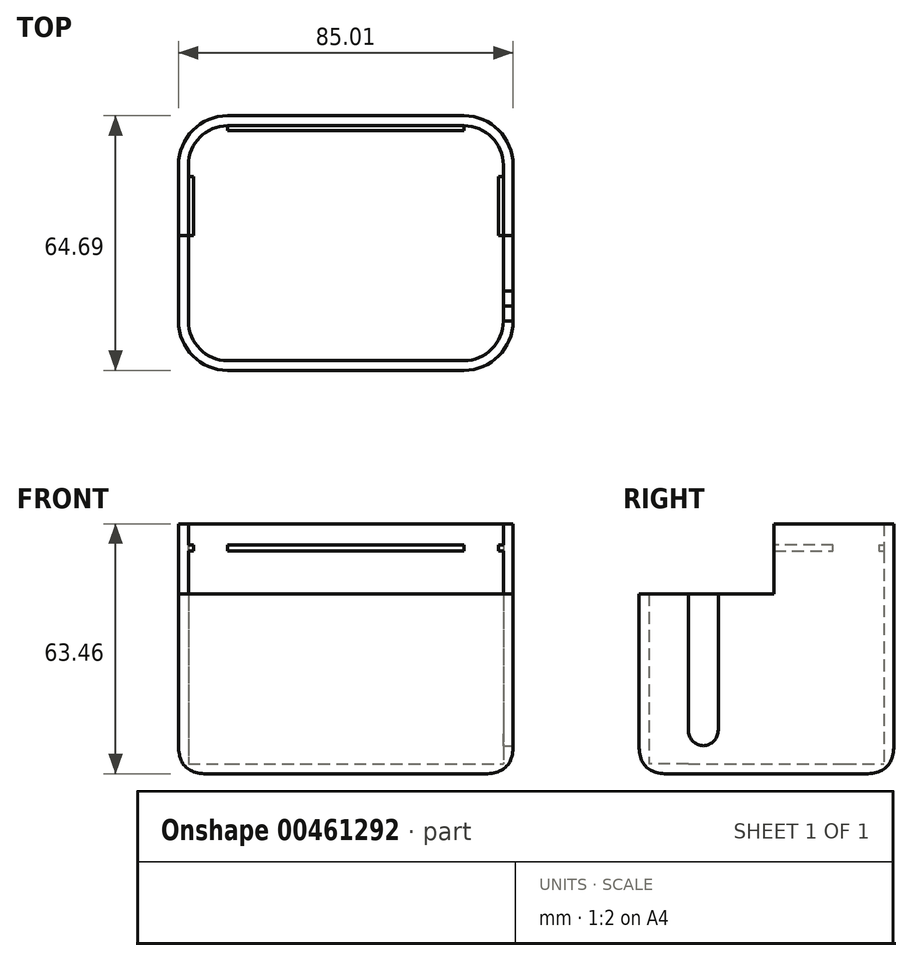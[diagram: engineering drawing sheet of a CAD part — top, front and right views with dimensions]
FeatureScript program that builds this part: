
annotation { "Feature Type Name" : "Feature", "Feature Type Description" : "" }
export const myFeature = defineFeature(function(context is Context, id is Id, definition is map)
    precondition{}
    {
        {
            var Q0;
            Q0=qCreatedBy(makeId("Top.planeOp"),FACE);
            var sketch = newSketch(context, id + "F0", { "sketchPlane" : qUnion([Q0])});
            skLineSegment(sketch, "E0.bottom", {"start": v(10, 0) * mm, "end": v(70.01, 0) * mm});
            skLineSegment(sketch, "E0.top", {"start": v(10, 59.7) * mm, "end": v(70.01, 59.7) * mm});
            skLineSegment(sketch, "E0.left", {"start": v(0, 10) * mm, "end": v(0, 49.7) * mm});
            skLineSegment(sketch, "E0.right", {"start": v(80.01, 10) * mm, "end": v(80.01, 49.7) * mm});
            skPoint(sketch, "E1.visualSharp", {"position": v(0, 59.7) * mm});
            skArc(sketch, "E1.filletArc", {"start": v(10, 59.7) * mm, "mid": v(2.93, 56.76) * mm, "end": v(0, 49.7) * mm});
            skPoint(sketch, "E2.visualSharp", {"position": v(0, 0) * mm});
            skArc(sketch, "E2.filletArc", {"start": v(0, 10) * mm, "mid": v(2.93, 2.93) * mm, "end": v(10, 0) * mm});
            skPoint(sketch, "E3.visualSharp", {"position": v(80.01, 0) * mm});
            skArc(sketch, "E3.filletArc", {"start": v(70.01, 0) * mm, "mid": v(77.08, 2.93) * mm, "end": v(80.01, 10) * mm});
            skPoint(sketch, "E4.visualSharp", {"position": v(80, 59.7) * mm});
            skArc(sketch, "E4.filletArc", {"start": v(80, 49.7) * mm, "mid": v(77.08, 56.76) * mm, "end": v(70.01, 59.7) * mm});
            skSolve(sketch);
        }
        {
            var Q0;
            Q0=makeQuery(id+"F0.imprint","IMPRINT",FACE,{"disambiguationData":[TD([[makeQuery(id+"F0.imprint","IMPRINT",EDGE,{"derivedFrom":sQuery(id+"F0.wireOp",EDGE,"E0.bottom")}),1.0]])]});
            extrude(context, id + "F1", {"entities" : qUnion([Q0]), "depth" : 60.96 * mm});
        }
        {
            var Q0;
            Q0=makeQuery(id+"F1.opExtrude","CAP_FACE",FACE,{"disambiguationData":[OSD([sQuery(id+"F0.wireOp",EDGE,"E0.bottom"),sQuery(id+"F0.wireOp",EDGE,"E0.top"),sQuery(id+"F0.wireOp",EDGE,"E0.left"),sQuery(id+"F0.wireOp",EDGE,"E0.right")])],"isStart":false});
            shell(context, id + "F2", {"entities" : qUnion([Q0]), "thickness" : 2.5 * mm, "oppositeDirection" : true});
        }
        {
            var Q0;
            Q0=makeQuery(id+"F1.opExtrude","CAP_FACE",FACE,{"disambiguationData":[OSD([sQuery(id+"F0.wireOp",EDGE,"E0.bottom"),sQuery(id+"F0.wireOp",EDGE,"E0.top"),sQuery(id+"F0.wireOp",EDGE,"E0.left"),sQuery(id+"F0.wireOp",EDGE,"E0.right"),sQuery(id+"F0.wireOp",EDGE,"E1.filletArc"),sQuery(id+"F0.wireOp",EDGE,"E2.filletArc"),sQuery(id+"F0.wireOp",EDGE,"E3.filletArc"),sQuery(id+"F0.wireOp",EDGE,"E4.filletArc")])],"isStart":true});
            fillet(context, id + "F3", {"entities" : qUnion([Q0]), "radius" : 7.1 * mm, "tangentPropagation" : true, "rho" : 0.5, "crossSection" : FilletCrossSection.CONIC, "allowEdgeOverflow" : false});
        }
        {
            var Q0;
            Q0=qCreatedBy(makeId("Right.planeOp"),FACE);
            var sketch = newSketch(context, id + "F4", { "sketchPlane" : qUnion([Q0])});
            skLineSegment(sketch, "E5", {"start": v(31.8, 60.96) * mm, "end": v(31.8, 43.18) * mm});
            skLineSegment(sketch, "E6", {"start": v(31.8, 43.18) * mm, "end": v(-2.5, 43.18) * mm});
            skLineSegment(sketch, "E7", {"start": v(-2.5, 43.18) * mm, "end": v(-2.5, 60.96) * mm});
            skLineSegment(sketch, "E8", {"start": v(-2.5, 60.96) * mm, "end": v(31.8, 60.96) * mm});
            skSolve(sketch);
        }
        {
            var Q0;
            Q0 = qSketchRegion(id + "F4", true);
            extrude(context, id + "F5", {"entities" : qUnion([Q0]), "operationType" : NewBodyOperationType.REMOVE, "endBound" : BoundingType.THROUGH_ALL, "depth" : 25 * mm, "hasSecondDirection" : true, "secondDirectionBound" : SecondDirectionBoundingType.THROUGH_ALL, "secondDirectionOppositeDirection" : true, "secondDirectionDepth" : 25 * mm});
        }
        {
            var Q0;
            Q0=makeQuery(id+"F2.opShell","OFFSET_FACE",FACE,{"disambiguationData":[OSD([sQuery(id+"F0.wireOp",EDGE,"E0.left")])]});
            var sketch = newSketch(context, id + "F6", { "sketchPlane" : qUnion([Q0])});
            skLineSegment(sketch, "E9.top", {"start": v(31.8, 54.1) * mm, "end": v(46.8, 54.1) * mm});
            skLineSegment(sketch, "E9.left", {"start": v(31.8, 54.1) * mm, "end": v(31.8, 55.63) * mm});
            skLineSegment(sketch, "E9.right", {"start": v(46.8, 54.1) * mm, "end": v(46.8, 55.63) * mm});
            skPoint(sketch, "E10", {"position": v(46.8, 54.86) * mm});
            skLineSegment(sketch, "E11", {"start": v(31.8, 55.63) * mm, "end": v(46.8, 55.63) * mm});
            skPoint(sketch, "E12", {"position": v(31.8, 54.86) * mm});
            skSolve(sketch);
        }
        {
            var Q0;
            Q0 = qSketchRegion(id + "F6", true);
            extrude(context, id + "F7", {"entities" : qUnion([Q0]), "operationType" : NewBodyOperationType.ADD, "endBound" : BoundingType.UP_TO_NEXT, "depth" : 25 * mm});
        }
        {
            var Q0;
            Q0=makeQuery(id+"F7.opExtrude","SWEPT_FACE",FACE,{"disambiguationData":[OSD([sQuery(id+"F6.wireOp",EDGE,"E11")])]});
            var sketch = newSketch(context, id + "F8", { "sketchPlane" : qUnion([Q0])});
            skLineSegment(sketch, "E13.bottom", {"start": v(1.27, 46.8) * mm, "end": v(78.74, 46.8) * mm});
            skLineSegment(sketch, "E13.top", {"start": v(1.27, 31.8) * mm, "end": v(78.74, 31.8) * mm});
            skLineSegment(sketch, "E13.left", {"start": v(1.27, 46.8) * mm, "end": v(1.27, 31.8) * mm});
            skLineSegment(sketch, "E13.right", {"start": v(78.74, 46.8) * mm, "end": v(78.74, 31.8) * mm});
            skSolve(sketch);
        }
        {
            var Q0;
            Q0 = qSketchRegion(id + "F8", true);
            extrude(context, id + "F9", {"entities" : qUnion([Q0]), "operationType" : NewBodyOperationType.REMOVE, "endBound" : BoundingType.UP_TO_NEXT, "oppositeDirection" : true, "depth" : 25 * mm});
        }
        {
            var Q0;
            Q0=makeQuery(id+"F2.opShell","OFFSET_FACE",FACE,{"disambiguationData":[OSD([sQuery(id+"F0.wireOp",EDGE,"E0.top")])]});
            var sketch = newSketch(context, id + "F10", { "sketchPlane" : qUnion([Q0])});
            skLineSegment(sketch, "E14", {"start": v(10, 54.86) * mm, "end": v(70.01, 54.86) * mm});
            skLineSegment(sketch, "E15.bottom", {"start": v(70.01, 54.1) * mm, "end": v(10, 54.1) * mm});
            skLineSegment(sketch, "E15.top", {"start": v(70.01, 55.63) * mm, "end": v(10, 55.63) * mm});
            skLineSegment(sketch, "E15.left", {"start": v(70.01, 55.63) * mm, "end": v(70.01, 54.1) * mm});
            skLineSegment(sketch, "E15.right", {"start": v(10, 55.63) * mm, "end": v(10, 54.1) * mm});
            skPoint(sketch, "E15.middle", {"position": v(40, 54.86) * mm});
            skSolve(sketch);
        }
        {
            var Q0;
            Q0 = qSketchRegion(id + "F10", true);
            extrude(context, id + "F11", {"entities" : qUnion([Q0]), "operationType" : NewBodyOperationType.ADD, "depth" : 1.27 * mm});
        }
        {
            var Q0;
            Q0=makeQuery(id+"F1.opExtrude","SWEPT_FACE",FACE,{"disambiguationData":[OSD([sQuery(id+"F0.wireOp",EDGE,"E0.right")])]});
            var sketch = newSketch(context, id + "F12", { "sketchPlane" : qUnion([Q0])});
            skLineSegment(sketch, "E16.bottom", {"start": v(13.62, 4.6) * mm, "end": v(14, 4.6) * mm});
            skLineSegment(sketch, "E16.top", {"start": v(10, 43.18) * mm, "end": v(17.62, 43.18) * mm});
            skLineSegment(sketch, "E16.left", {"start": v(10, 8.6) * mm, "end": v(10, 43.18) * mm});
            skLineSegment(sketch, "E16.right", {"start": v(17.62, 8.6) * mm, "end": v(17.62, 43.18) * mm});
            skPoint(sketch, "E17.visualSharp", {"position": v(10, 4.6) * mm});
            skArc(sketch, "E17.filletArc", {"start": v(10, 8.6) * mm, "mid": v(11.17, 5.77) * mm, "end": v(14, 4.6) * mm});
            skPoint(sketch, "E18.visualSharp", {"position": v(17.62, 4.6) * mm});
            skArc(sketch, "E18.filletArc", {"start": v(13.62, 4.6) * mm, "mid": v(16.45, 5.77) * mm, "end": v(17.62, 8.6) * mm});
            skSolve(sketch);
        }
        {
            var Q0;
            Q0 = qSketchRegion(id + "F12", true);
            extrude(context, id + "F13", {"entities" : qUnion([Q0]), "operationType" : NewBodyOperationType.REMOVE, "oppositeDirection" : true, "depth" : 25 * mm});
        }
    });
